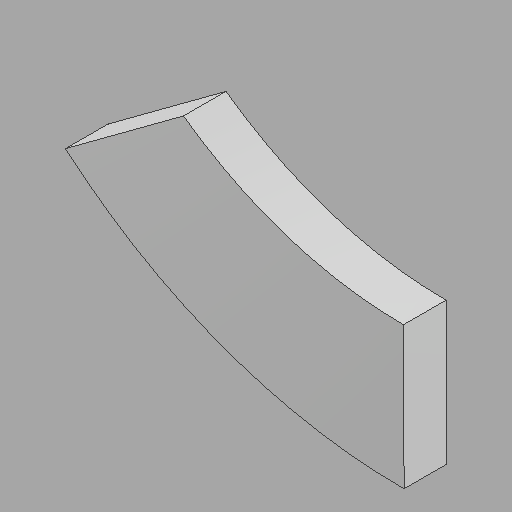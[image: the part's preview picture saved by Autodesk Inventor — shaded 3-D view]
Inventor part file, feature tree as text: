
AUTODESK INVENTOR PART (.ipt)
format: ipt  version: 2022.1 (Build 261234020, 234B)  size: 90,112 bytes
history: imported  units: in
note: dims shown in document units (in); Inventor stores cm internally (conversion verified against a paired STEP export)
features: imported_body x1
ambient origin geometry x8: Origin, YZ Plane, XZ Plane, XY Plane, X Axis, Y Axis, Z Axis, Center Point
bodies: Solid1 (imported_parasolid)
feature tree (1):
  imported_body  NMx_Import_Brep_tag  [imported B-rep: ~6 faces, bbox_mm=[1213.186396, 761.386567, 152.4]]
